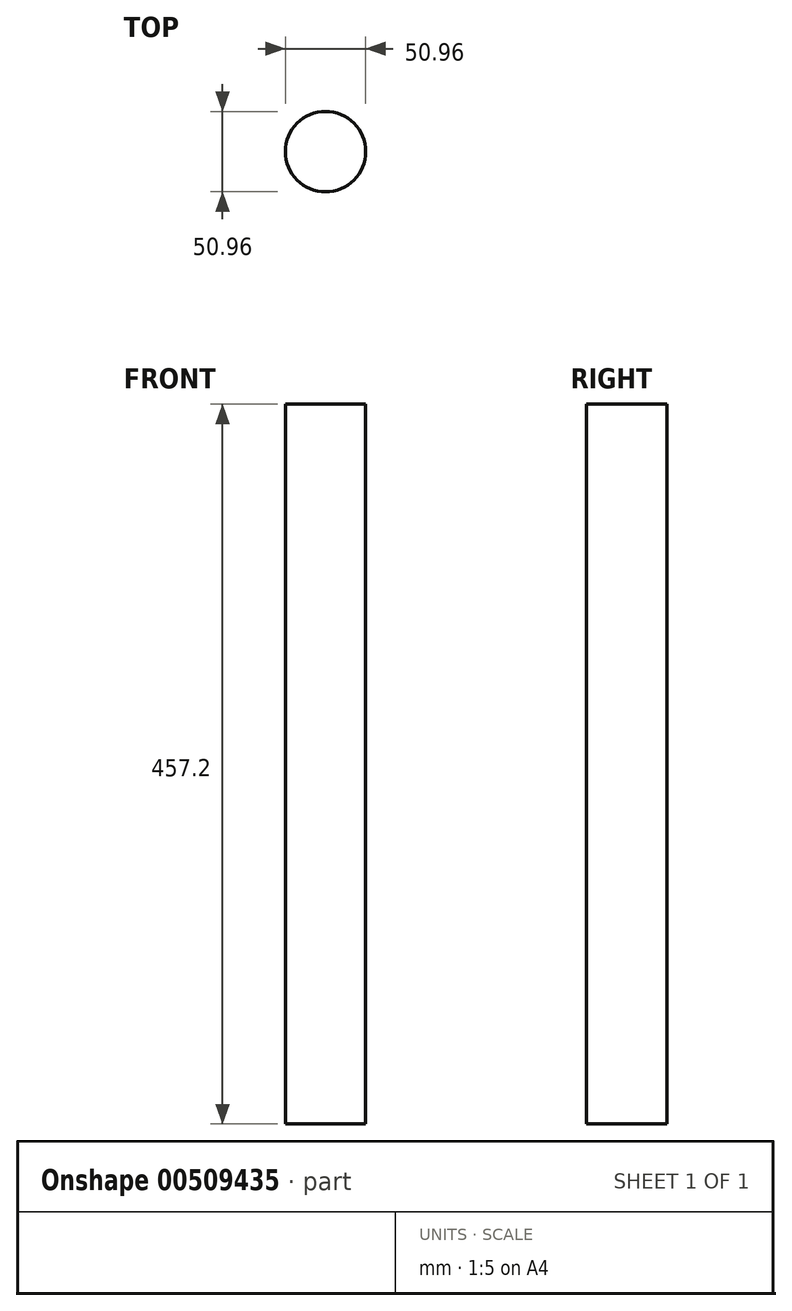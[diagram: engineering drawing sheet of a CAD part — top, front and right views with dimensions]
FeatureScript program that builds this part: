
annotation { "Feature Type Name" : "Feature", "Feature Type Description" : "" }
export const myFeature = defineFeature(function(context is Context, id is Id, definition is map)
    precondition{}
    {
        {
            var Q0;
            Q0=qCreatedBy(makeId("Top.planeOp"),FACE);
            var sketch = newSketch(context, id + "F0", { "sketchPlane" : qUnion([Q0])});
            skCircle(sketch, "E0", {"center": v(0, 0) * mm, "radius": 25.48 * mm});
            skSolve(sketch);
        }
        {
            var Q0;
            Q0 = qSketchRegion(id + "F0", true);
            extrude(context, id + "F1", {"entities" : qUnion([Q0]), "depth" : 457.2 * mm});
        }
    });
